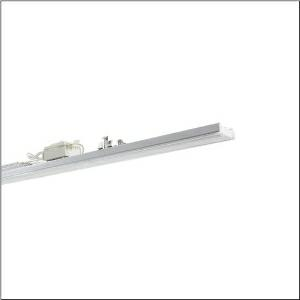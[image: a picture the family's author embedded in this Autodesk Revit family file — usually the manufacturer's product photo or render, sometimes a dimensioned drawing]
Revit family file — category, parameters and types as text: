
# Revit family: licross_21_recessed_mo_52te12dv4fxgd
name_source: partatom
category: Lighting Fixtures
units: mm (PartAtom-declared; Revit-internal decimal feet)

## family parameters
Cut with Voids When Loaded = No
Host = Face
Light Source = No
Part Type = Normal
Room Calculation Point = No
Round Connector Dimension = Use Diameter
Shared = No

## types (1)
- --- (1 x LED, 15420 lm, 85.3 W, 4000K)
    Apparent Load = 85 VA
    CIE Flux Codes = 72 92 99 100 100
    Color Rendering = 80
    Color Temperature = 4000K
    Default Elevation = 1800 mm
    Description = Licross 21 Recessed MO, luminaire insert, of sheet steel, galvanised, coil coated, white, length: 2.250mm, width: 66mm, height: 67mm, LED rated luminous flux: 15.420lm, light colour: 840, SDCM (Standard Deviation of Colour Matching)MacAdam ≤ 3 SDCM (initial), control gear: DALI 2 (for two DALI lines), with plug, 6-pole, with phase selection, mains connection: 220..240V, AC/DC, 0/50..60Hz, rated input power: 85W, without changeover relay, for emergency light function, for central battery installations according to EN 60598-2-22, internal wiring halogen-free, primary optical cover: cover, of PMMA, light emission: direct distribution, primary light characteristic: symmetric, protection rating (complete): IP54, insulation class (complete): insulation class I (protective earthing), certification: CE, ENEC, VDE, UKCA, protection symbol: D if used in an environment with non-conductive dust loads with corresponding accessories, impact resistance: IK06, permissible ambient temperature for indoor applications: -25..+35°C, standard: EN 60598-2-22, corresponds to IFS (International Featured Standards) requirements for safety and quality in the food industry, reducing of maximum allowable ambient temperature of 5°C with ceiling mounting, LABS conformity tested according to VDMA 24364:2018-05, The light source and the operating device comply with the requirements of the Ecodesign Regulation (EU) 2019/2020 and are replaceable in accordance with this regulation, packaging unit: 1 piece
    Height = 58 mm
    Lamp = 1 x LED
    Lamp Light Flux = 15420 lm
    Lamp Power = 85.3 W
    Lamp count = 1
    Length = 2250 mm
    Luminous efficacy = 181 lm/W
    Manufacturer = Siteco
    ModVariant = No
    Model = 52TE12DV4FXGD
    Mounting Place = Ceiling
    Mounting Type = Pendant
    Number of Poles = 1
    OnlyDefault = Yes
    Power Factor = 1
    Product Name = Licross 21 Recessed MO
    Product group = luminaire insert | ceiling pendant
    ProductGroupID = 901
    Protection Class = Protection class I
    Protection Degree = IP 54
    RLX_Detail_Level = 1
    RLX_Emergency_Light_Flux = 0 lm
    RLX_Emergency_Type = 0
    RLX_Emergency_Type_DB = No
    RlxData = <blob elided: 30073 chars, md5=2150d281>
    Socket = socket
    Standby Power = 0 W
    System Light Flux = 15420 lm
    System Power = 85 W
    Type Comments = : AC-mode, luminous flux: 100 % | dim-lin: 254 | 390 mA
    Type Image = l_1296930.jpg
    URL = http://relux.com
    VarID = @adj_113097
    Voltage = 0 V
    Weight = 0.00 kg
    Width = 66 mm

## geometry (parser evidence)
native form markers: Blend x4, Sweep x10
no freeform markers — native parametric forms only
